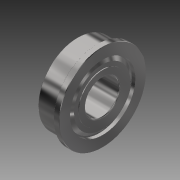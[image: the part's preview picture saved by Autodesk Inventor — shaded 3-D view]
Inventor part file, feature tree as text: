
AUTODESK INVENTOR PART (.ipt)
format: ipt  version: 2014 (Build 180170000, 170)  size: 381,440 bytes
history: native  units: in
note: dims shown in document units (in); Inventor stores cm internally (conversion verified against a paired STEP export)
features: other x4, imported_body x3, extrude x1, fillet x1, sketch x1
ambient origin geometry x8: Origin, YZ Plane, XZ Plane, XY Plane, X Axis, Y Axis, Z Axis, Center Point
bodies: Body1 (feature_tree), Body2 (feature_tree), Body3 (feature_tree)
feature tree (10):
  other  "FR6ZZ"
  other  "FR6ZZ1"
  extrude  "Extrusion1"  Depth=0.01in
  fillet  "Fillet1"  [1 undecoded]
  other  "FR6ZZ_1"
  other  "FR6ZZ_2"
  imported_body  "Base1"
  imported_body  "Base2"
  imported_body  "Base3"
  sketch  "Sketch1"  dims[d0=1.0in d1=0.0in d2=0.01in]
note: 1 required parameter value undecoded (feature->parameter linkage not recoverable at this tier; creation-order binding heuristic only, values carry confidence <= 0.55)
